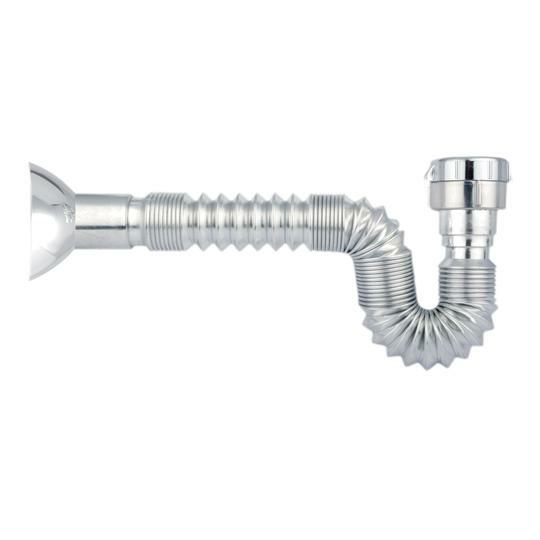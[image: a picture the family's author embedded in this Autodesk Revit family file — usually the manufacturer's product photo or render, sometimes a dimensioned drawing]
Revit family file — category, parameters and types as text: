
# Revit family: BIM_01-2907-211
name_source: partatom
category: Aparatos sanitarios
units: mm (PartAtom-declared; Revit-internal decimal feet)

## family parameters
Activar corte en vistas = No
Anfitrión = Cara
Compartido = No
Corte con vacíos al cargar = No
Cota de conector redondo = Usar diámetro
Mantener orientación de anotación = No
Número OmniClass = 23.31.11.00
Punto de cálculo de habitación = No
Tipo de pieza = Normal

## types (1)
- 01-2907-11
    Ancho = 47.5 mm
    Conexiones = Tubo para acople en tubería de 1¼'' ó 1½''
    Conexión AC = Sí
    Conexión AF = Sí
    Conexión de residuos = No
    Conexión de ventilación = No
    Consumo aproximado a 25 psi = 27
    Descripción = Sifon
    Diametro Externo = 1 1/2"
    Elevación por defecto = 0 mm  [stored 0 ft]
    Fabricante = Gricol
    Garantia Especifica = 20 Años
    Goteo de Sello = 63 ml/min
    Imagen de tipo = FOTO-SIFÓN EXPANSIBLE PLÁSTICO 1½ Ó 1¼ METALIZADO.jpg
    Largo expandido = 827 mm
    Link Ficha Tecnica = https://infotecnica.gricol.com
    Materiales del producto = Polipropileno, Caucho
    Modelo = 01-2907-11
    Plastico - ABS Cromado = Plastico ABS Cromado
    Plastico polipropileno gris = Plastico - polipropileno gris
    Product Name = SIFÓN EXPANSIBLE PLÁSTICO 1½ Ó 1¼
    Referente Normativo = NTC 5302, ASME A112.18.2 / CSA B125.2
    Resistencia a Corrosión = NTC 1156, Sal Neutral
    Sitio web = https://www.gricol.com
    Temperaturas de trabajo = de 19C° A 62C°
    Tipo de Uso = Domestico
    Torque de Conexioón = 20 Nm
    Tubo de desagüe = 1 1/2"
    Tubo macho pared = 1 1/4"
    URL = https://www.gricol.com
    largo Contraido = 315 mm

note: [stored X ft] marks values corroborated as IEEE doubles in the binary element streams (Revit-internal decimal feet)

## geometry (parser evidence)
native form markers: Blend x2, Sweep x3
no freeform markers — native parametric forms only
